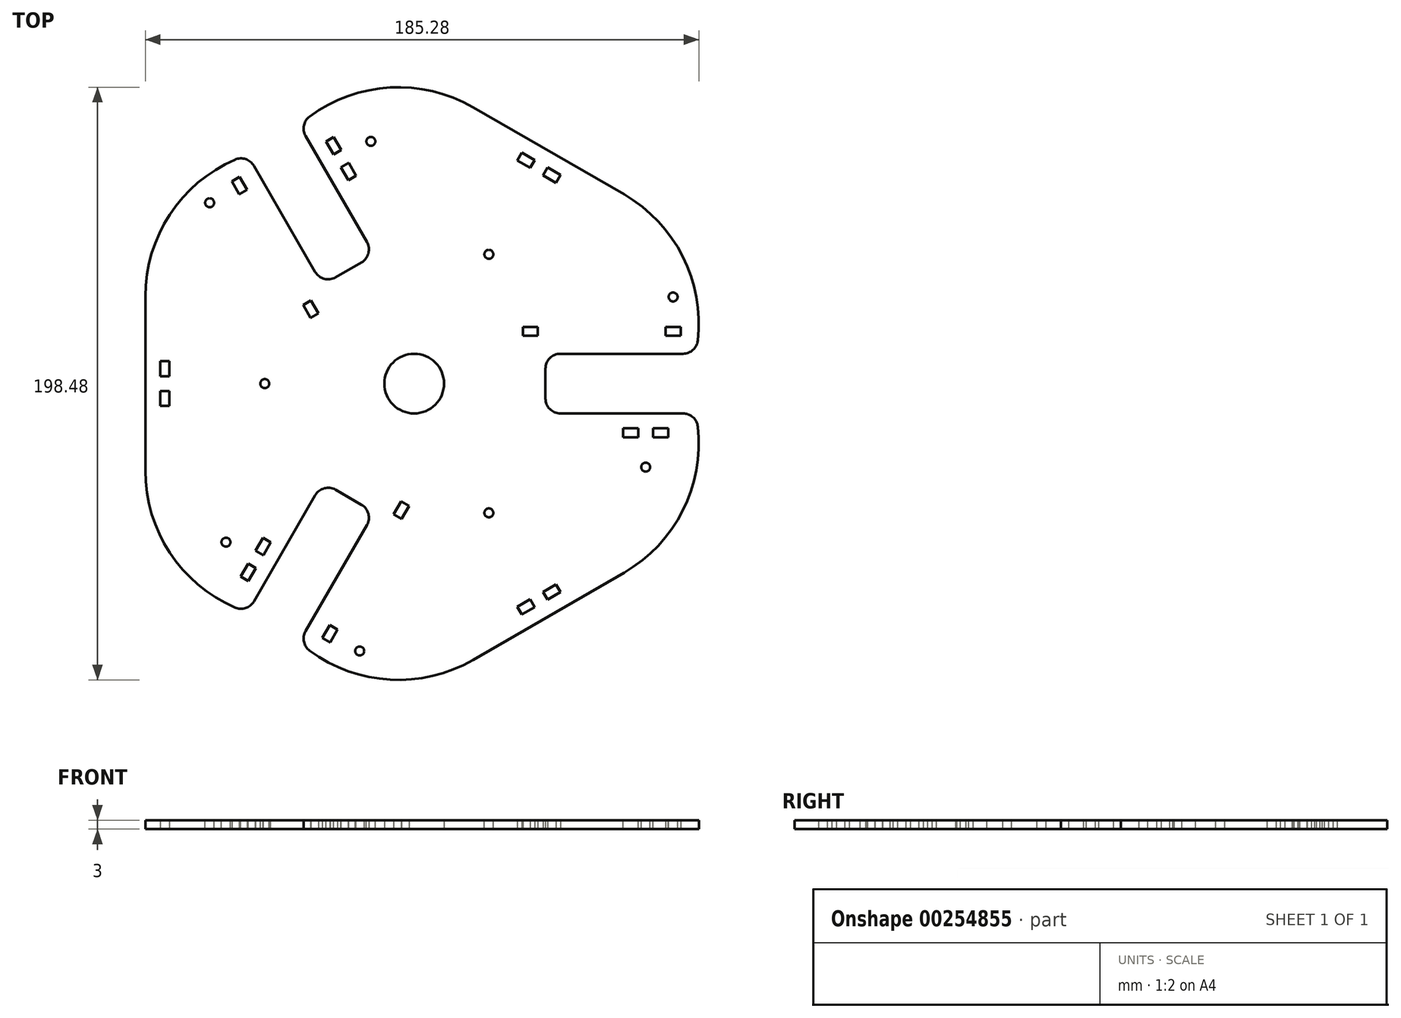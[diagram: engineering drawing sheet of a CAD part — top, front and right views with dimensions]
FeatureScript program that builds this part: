
annotation { "Feature Type Name" : "Feature", "Feature Type Description" : "" }
export const myFeature = defineFeature(function(context is Context, id is Id, definition is map)
    precondition{}
    {
        {
            var Q0;
            Q0=qCreatedBy(makeId("Top.planeOp"),FACE);
            var sketch = newSketch(context, id + "F0", { "sketchPlane" : qUnion([Q0])});
            skLineSegment(sketch, "E0", {"start": v(19.85, 17.5) * mm, "end": v(153.53, 17.5) * mm, "construction": true});
            skLineSegment(sketch, "E1.bottom", {"start": v(41.39, 16) * mm, "end": v(36.39, 16) * mm});
            skLineSegment(sketch, "E1.top", {"start": v(41.39, 19) * mm, "end": v(36.39, 19) * mm});
            skLineSegment(sketch, "E1.left", {"start": v(41.39, 16) * mm, "end": v(41.39, 19) * mm});
            skLineSegment(sketch, "E1.right", {"start": v(36.39, 16) * mm, "end": v(36.39, 19) * mm});
            skPoint(sketch, "E1.middle", {"position": v(38.89, 17.5) * mm});
            skLineSegment(sketch, "E2.bottom", {"start": v(89.19, 16) * mm, "end": v(84.19, 16) * mm});
            skLineSegment(sketch, "E2.top", {"start": v(89.19, 19) * mm, "end": v(84.19, 19) * mm});
            skLineSegment(sketch, "E2.left", {"start": v(89.19, 16) * mm, "end": v(89.19, 19) * mm});
            skLineSegment(sketch, "E2.right", {"start": v(84.19, 16) * mm, "end": v(84.19, 19) * mm});
            skPoint(sketch, "E2.middle", {"position": v(86.69, 17.5) * mm});
            skLineSegment(sketch, "E3", {"start": v(90, 10) * mm, "end": v(48.96, 10) * mm});
            skLineSegment(sketch, "E4", {"start": v(43.96, 5) * mm, "end": v(43.96, -5) * mm});
            skLineSegment(sketch, "E5", {"start": v(48.96, -10) * mm, "end": v(90, -10) * mm});
            skPoint(sketch, "E6.visualSharp", {"position": v(43.96, 10) * mm});
            skArc(sketch, "E6.filletArc", {"start": v(48.96, 10) * mm, "mid": v(45.42, 8.54) * mm, "end": v(43.96, 5) * mm});
            skPoint(sketch, "E7.visualSharp", {"position": v(43.96, -10) * mm});
            skArc(sketch, "E7.filletArc", {"start": v(43.96, -5) * mm, "mid": v(45.42, -8.54) * mm, "end": v(48.96, -10) * mm});
            skPoint(sketch, "E8.visualSharp", {"position": v(94.4, 59.99) * mm});
            skArc(sketch, "E8.filletArc", {"start": v(94.97, 14.44) * mm, "mid": v(89.92, 42.57) * mm, "end": v(70.28, 63.34) * mm});
            skPoint(sketch, "E9.visualSharp", {"position": v(94.34, 10) * mm});
            skArc(sketch, "E9.filletArc", {"start": v(90, 10) * mm, "mid": v(93.33, 11.27) * mm, "end": v(94.97, 14.44) * mm});
            skPoint(sketch, "E10.visualSharp", {"position": v(102.08, -10) * mm});
            skArc(sketch, "E10.filletArc", {"start": v(94.97, -14.44) * mm, "mid": v(93.33, -11.27) * mm, "end": v(90, -10) * mm});
            skLineSegment(sketch, "E11", {"start": v(0, 0) * mm, "end": v(57.44, 99.5) * mm, "construction": true});
            skLineSegment(sketch, "E12", {"start": v(0, 0) * mm, "end": v(55.62, -96.34) * mm, "construction": true});
            skLineSegment(sketch, "E13", {"start": v(70.28, -63.34) * mm, "end": v(45, -77.94) * mm});
            skLineSegment(sketch, "E14", {"start": v(70.28, 63.34) * mm, "end": v(45, 77.94) * mm});
            skPoint(sketch, "E15.visualSharp", {"position": v(93.21, -50.1) * mm});
            skArc(sketch, "E15.filletArc", {"start": v(70.28, -63.34) * mm, "mid": v(89.92, -42.57) * mm, "end": v(94.97, -14.44) * mm});
            skLineSegment(sketch, "E16.1.0", {"start": v(-90, 29.2) * mm, "end": v(-90, 0) * mm});
            skArc(sketch, "E16.1.1", {"start": v(-59.99, 75.03) * mm, "mid": v(-81.83, 56.59) * mm, "end": v(-90, 29.2) * mm});
            skArc(sketch, "E16.1.2", {"start": v(-53.66, 72.94) * mm, "mid": v(-56.43, 75.2) * mm, "end": v(-59.99, 75.03) * mm});
            skLineSegment(sketch, "E16.1.3", {"start": v(-53.66, 72.94) * mm, "end": v(-33.14, 37.4) * mm});
            skArc(sketch, "E16.1.4", {"start": v(-33.14, 37.4) * mm, "mid": v(-30.1, 35.07) * mm, "end": v(-26.3, 35.57) * mm});
            skLineSegment(sketch, "E16.1.5", {"start": v(-26.3, 35.57) * mm, "end": v(-17.65, 40.57) * mm});
            skArc(sketch, "E16.1.6", {"start": v(-17.65, 40.57) * mm, "mid": v(-15.32, 43.6) * mm, "end": v(-15.82, 47.4) * mm});
            skLineSegment(sketch, "E16.1.7", {"start": v(-15.82, 47.4) * mm, "end": v(-36.34, 82.94) * mm});
            skArc(sketch, "E16.1.8", {"start": v(19.72, 92.54) * mm, "mid": v(-8.09, 99.16) * mm, "end": v(-34.98, 89.46) * mm});
            skArc(sketch, "E16.1.9", {"start": v(-34.98, 89.46) * mm, "mid": v(-36.9, 86.46) * mm, "end": v(-36.34, 82.94) * mm});
            skLineSegment(sketch, "E16.1.10", {"start": v(-58.45, 69.24) * mm, "end": v(-55.95, 64.91) * mm});
            skLineSegment(sketch, "E16.1.11", {"start": v(-55.95, 64.91) * mm, "end": v(-58.55, 63.41) * mm});
            skLineSegment(sketch, "E16.1.12", {"start": v(-61.05, 67.74) * mm, "end": v(-58.55, 63.41) * mm});
            skLineSegment(sketch, "E16.1.13", {"start": v(-58.45, 69.24) * mm, "end": v(-61.05, 67.74) * mm});
            skLineSegment(sketch, "E16.1.14", {"start": v(-34.55, 27.84) * mm, "end": v(-37.15, 26.34) * mm});
            skLineSegment(sketch, "E16.1.15", {"start": v(-34.55, 27.84) * mm, "end": v(-32.05, 23.51) * mm});
            skLineSegment(sketch, "E16.1.16", {"start": v(-32.05, 23.51) * mm, "end": v(-34.65, 22.01) * mm});
            skLineSegment(sketch, "E16.1.17", {"start": v(-37.15, 26.34) * mm, "end": v(-34.65, 22.01) * mm});
            skLineSegment(sketch, "E16.1.18", {"start": v(19.72, 92.54) * mm, "end": v(45, 77.94) * mm});
            skLineSegment(sketch, "E16.2.0", {"start": v(19.72, -92.54) * mm, "end": v(45, -77.94) * mm});
            skArc(sketch, "E16.2.1", {"start": v(-34.98, -89.46) * mm, "mid": v(-8.09, -99.16) * mm, "end": v(19.72, -92.54) * mm});
            skArc(sketch, "E16.2.2", {"start": v(-36.34, -82.94) * mm, "mid": v(-36.9, -86.46) * mm, "end": v(-34.98, -89.46) * mm});
            skLineSegment(sketch, "E16.2.3", {"start": v(-36.34, -82.94) * mm, "end": v(-15.82, -47.4) * mm});
            skArc(sketch, "E16.2.4", {"start": v(-15.82, -47.4) * mm, "mid": v(-15.32, -43.6) * mm, "end": v(-17.65, -40.57) * mm});
            skLineSegment(sketch, "E16.2.5", {"start": v(-17.65, -40.57) * mm, "end": v(-26.3, -35.57) * mm});
            skArc(sketch, "E16.2.6", {"start": v(-26.3, -35.57) * mm, "mid": v(-30.1, -35.07) * mm, "end": v(-33.14, -37.4) * mm});
            skLineSegment(sketch, "E16.2.7", {"start": v(-33.14, -37.4) * mm, "end": v(-53.66, -72.94) * mm});
            skArc(sketch, "E16.2.8", {"start": v(-90, -29.2) * mm, "mid": v(-81.83, -56.59) * mm, "end": v(-59.99, -75.03) * mm});
            skArc(sketch, "E16.2.9", {"start": v(-59.99, -75.03) * mm, "mid": v(-56.43, -75.2) * mm, "end": v(-53.66, -72.94) * mm});
            skLineSegment(sketch, "E16.2.10", {"start": v(-30.74, -85.24) * mm, "end": v(-28.24, -80.91) * mm});
            skLineSegment(sketch, "E16.2.11", {"start": v(-28.24, -80.91) * mm, "end": v(-25.64, -82.41) * mm});
            skLineSegment(sketch, "E16.2.12", {"start": v(-28.14, -86.74) * mm, "end": v(-25.64, -82.41) * mm});
            skLineSegment(sketch, "E16.2.13", {"start": v(-30.74, -85.24) * mm, "end": v(-28.14, -86.74) * mm});
            skLineSegment(sketch, "E16.2.14", {"start": v(-6.84, -43.84) * mm, "end": v(-4.24, -45.34) * mm});
            skLineSegment(sketch, "E16.2.15", {"start": v(-6.84, -43.84) * mm, "end": v(-4.34, -39.51) * mm});
            skLineSegment(sketch, "E16.2.16", {"start": v(-4.34, -39.51) * mm, "end": v(-1.74, -41.01) * mm});
            skLineSegment(sketch, "E16.2.17", {"start": v(-4.24, -45.34) * mm, "end": v(-1.74, -41.01) * mm});
            skLineSegment(sketch, "E16.2.18", {"start": v(-90, -29.2) * mm, "end": v(-90, 0) * mm});
            skPoint(sketch, "E16.center", {"position": v(0, 0) * mm});
            skCircle(sketch, "E17", {"center": v(0, 0) * mm, "radius": 10 * mm});
            skLineSegment(sketch, "E18.bottom", {"start": v(-85, 7.5) * mm, "end": v(-82, 7.5) * mm});
            skLineSegment(sketch, "E18.top", {"start": v(-85, 2.5) * mm, "end": v(-82, 2.5) * mm});
            skLineSegment(sketch, "E18.left", {"start": v(-85, 7.5) * mm, "end": v(-85, 2.5) * mm});
            skLineSegment(sketch, "E18.right", {"start": v(-82, 7.5) * mm, "end": v(-82, 2.5) * mm});
            skLineSegment(sketch, "E19.bottom", {"start": v(-85, -2.5) * mm, "end": v(-82, -2.5) * mm});
            skLineSegment(sketch, "E19.top", {"start": v(-85, -7.5) * mm, "end": v(-82, -7.5) * mm});
            skLineSegment(sketch, "E19.left", {"start": v(-85, -2.5) * mm, "end": v(-85, -7.5) * mm});
            skLineSegment(sketch, "E19.right", {"start": v(-82, -2.5) * mm, "end": v(-82, -7.5) * mm});
            skLineSegment(sketch, "E20.1.0", {"start": v(36, -77.36) * mm, "end": v(34.5, -74.76) * mm});
            skLineSegment(sketch, "E20.1.1", {"start": v(36, -77.36) * mm, "end": v(40.33, -74.86) * mm});
            skLineSegment(sketch, "E20.1.2", {"start": v(34.5, -74.76) * mm, "end": v(38.83, -72.26) * mm});
            skLineSegment(sketch, "E20.1.3", {"start": v(40.33, -74.86) * mm, "end": v(38.83, -72.26) * mm});
            skLineSegment(sketch, "E20.1.4", {"start": v(44.67, -72.36) * mm, "end": v(43.17, -69.76) * mm});
            skLineSegment(sketch, "E20.1.5", {"start": v(44.67, -72.36) * mm, "end": v(49, -69.86) * mm});
            skLineSegment(sketch, "E20.1.6", {"start": v(49, -69.86) * mm, "end": v(47.5, -67.26) * mm});
            skLineSegment(sketch, "E20.1.7", {"start": v(43.17, -69.76) * mm, "end": v(47.5, -67.26) * mm});
            skLineSegment(sketch, "E20.2.0", {"start": v(49, 69.86) * mm, "end": v(47.5, 67.26) * mm});
            skLineSegment(sketch, "E20.2.1", {"start": v(49, 69.86) * mm, "end": v(44.67, 72.36) * mm});
            skLineSegment(sketch, "E20.2.2", {"start": v(47.5, 67.26) * mm, "end": v(43.17, 69.76) * mm});
            skLineSegment(sketch, "E20.2.3", {"start": v(44.67, 72.36) * mm, "end": v(43.17, 69.76) * mm});
            skLineSegment(sketch, "E20.2.4", {"start": v(40.33, 74.86) * mm, "end": v(38.83, 72.26) * mm});
            skLineSegment(sketch, "E20.2.5", {"start": v(40.33, 74.86) * mm, "end": v(36, 77.36) * mm});
            skLineSegment(sketch, "E20.2.6", {"start": v(36, 77.36) * mm, "end": v(34.5, 74.76) * mm});
            skLineSegment(sketch, "E20.2.7", {"start": v(38.83, 72.26) * mm, "end": v(34.5, 74.76) * mm});
            skSolve(sketch);
        }
        {
            var Q0;
            Q0 = qSketchRegion(id + "F0", true);
            extrude(context, id + "F1", {"entities" : qUnion([Q0]), "depth" : 3 * mm});
        }
        {
            var Q0;
            Q0=makeQuery(id+"F1.opExtrude","CAP_FACE",FACE,{"disambiguationData":[OSD([sQuery(id+"F0.wireOp",EDGE,"E1.bottom"),sQuery(id+"F0.wireOp",EDGE,"E1.top"),sQuery(id+"F0.wireOp",EDGE,"E1.left"),sQuery(id+"F0.wireOp",EDGE,"E1.right"),sQuery(id+"F0.wireOp",EDGE,"E2.bottom"),sQuery(id+"F0.wireOp",EDGE,"E2.top"),sQuery(id+"F0.wireOp",EDGE,"E2.left"),sQuery(id+"F0.wireOp",EDGE,"E2.right"),sQuery(id+"F0.wireOp",EDGE,"E3"),sQuery(id+"F0.wireOp",EDGE,"E4"),sQuery(id+"F0.wireOp",EDGE,"E5"),sQuery(id+"F0.wireOp",EDGE,"E6.filletArc"),sQuery(id+"F0.wireOp",EDGE,"E7.filletArc"),sQuery(id+"F0.wireOp",EDGE,"E8.filletArc"),sQuery(id+"F0.wireOp",EDGE,"E9.filletArc"),sQuery(id+"F0.wireOp",EDGE,"E10.filletArc"),sQuery(id+"F0.wireOp",EDGE,"E13"),sQuery(id+"F0.wireOp",EDGE,"E14"),sQuery(id+"F0.wireOp",EDGE,"E15.filletArc"),sQuery(id+"F0.wireOp",EDGE,"E16.1.0"),sQuery(id+"F0.wireOp",EDGE,"E16.1.1"),sQuery(id+"F0.wireOp",EDGE,"E16.1.2"),sQuery(id+"F0.wireOp",EDGE,"E16.1.3"),sQuery(id+"F0.wireOp",EDGE,"E16.1.4"),sQuery(id+"F0.wireOp",EDGE,"E16.1.5"),sQuery(id+"F0.wireOp",EDGE,"E16.1.6"),sQuery(id+"F0.wireOp",EDGE,"E16.1.7"),sQuery(id+"F0.wireOp",EDGE,"E16.1.8"),sQuery(id+"F0.wireOp",EDGE,"E16.1.9"),sQuery(id+"F0.wireOp",EDGE,"E16.1.10"),sQuery(id+"F0.wireOp",EDGE,"E16.1.11"),sQuery(id+"F0.wireOp",EDGE,"E16.1.12"),sQuery(id+"F0.wireOp",EDGE,"E16.1.13"),sQuery(id+"F0.wireOp",EDGE,"E16.1.14"),sQuery(id+"F0.wireOp",EDGE,"E16.1.15"),sQuery(id+"F0.wireOp",EDGE,"E16.1.16"),sQuery(id+"F0.wireOp",EDGE,"E16.1.17"),sQuery(id+"F0.wireOp",EDGE,"E16.1.18"),sQuery(id+"F0.wireOp",EDGE,"E16.2.0"),sQuery(id+"F0.wireOp",EDGE,"E16.2.1"),sQuery(id+"F0.wireOp",EDGE,"E16.2.2"),sQuery(id+"F0.wireOp",EDGE,"E16.2.3"),sQuery(id+"F0.wireOp",EDGE,"E16.2.4"),sQuery(id+"F0.wireOp",EDGE,"E16.2.5"),sQuery(id+"F0.wireOp",EDGE,"E16.2.6"),sQuery(id+"F0.wireOp",EDGE,"E16.2.7"),sQuery(id+"F0.wireOp",EDGE,"E16.2.8"),sQuery(id+"F0.wireOp",EDGE,"E16.2.9"),sQuery(id+"F0.wireOp",EDGE,"E16.2.10"),sQuery(id+"F0.wireOp",EDGE,"E16.2.11"),sQuery(id+"F0.wireOp",EDGE,"E16.2.12"),sQuery(id+"F0.wireOp",EDGE,"E16.2.13"),sQuery(id+"F0.wireOp",EDGE,"E16.2.14"),sQuery(id+"F0.wireOp",EDGE,"E16.2.15"),sQuery(id+"F0.wireOp",EDGE,"E16.2.16"),sQuery(id+"F0.wireOp",EDGE,"E16.2.17"),sQuery(id+"F0.wireOp",EDGE,"E16.2.18"),sQuery(id+"F0.wireOp",EDGE,"E17"),sQuery(id+"F0.wireOp",EDGE,"E18.bottom"),sQuery(id+"F0.wireOp",EDGE,"E18.top"),sQuery(id+"F0.wireOp",EDGE,"E18.left"),sQuery(id+"F0.wireOp",EDGE,"E18.right"),sQuery(id+"F0.wireOp",EDGE,"E19.bottom"),sQuery(id+"F0.wireOp",EDGE,"E19.top"),sQuery(id+"F0.wireOp",EDGE,"E19.left"),sQuery(id+"F0.wireOp",EDGE,"E19.right"),sQuery(id+"F0.wireOp",EDGE,"E20.1.0"),sQuery(id+"F0.wireOp",EDGE,"E20.1.1"),sQuery(id+"F0.wireOp",EDGE,"E20.1.2"),sQuery(id+"F0.wireOp",EDGE,"E20.1.3"),sQuery(id+"F0.wireOp",EDGE,"E20.1.4"),sQuery(id+"F0.wireOp",EDGE,"E20.1.5"),sQuery(id+"F0.wireOp",EDGE,"E20.1.6"),sQuery(id+"F0.wireOp",EDGE,"E20.1.7"),sQuery(id+"F0.wireOp",EDGE,"E20.2.0"),sQuery(id+"F0.wireOp",EDGE,"E20.2.1"),sQuery(id+"F0.wireOp",EDGE,"E20.2.2"),sQuery(id+"F0.wireOp",EDGE,"E20.2.3"),sQuery(id+"F0.wireOp",EDGE,"E20.2.4"),sQuery(id+"F0.wireOp",EDGE,"E20.2.5"),sQuery(id+"F0.wireOp",EDGE,"E20.2.6"),sQuery(id+"F0.wireOp",EDGE,"E20.2.7")])],"isStart":false});
            var sketch = newSketch(context, id + "F2", { "sketchPlane" : qUnion([Q0])});
            skCircle(sketch, "E21", {"center": v(-50, 0) * mm, "radius": 1.5 * mm});
            skCircle(sketch, "E22.1.0", {"center": v(25, -43.3) * mm, "radius": 1.5 * mm});
            skCircle(sketch, "E22.2.0", {"center": v(25, 43.3) * mm, "radius": 1.5 * mm});
            skPoint(sketch, "E22.center", {"position": v(0, 0) * mm});
            skCircle(sketch, "E23", {"center": v(86.69, 29) * mm, "radius": 1.5 * mm});
            skPoint(sketch, "E23.centerSnap0", {"position": v(86.69, 19) * mm});
            skCircle(sketch, "E24.1.0", {"center": v(-68.46, 60.58) * mm, "radius": 1.5 * mm});
            skCircle(sketch, "E24.2.0", {"center": v(-18.23, -89.58) * mm, "radius": 1.5 * mm});
            skLineSegment(sketch, "E25.bottom", {"start": v(70, -15) * mm, "end": v(75, -15) * mm});
            skLineSegment(sketch, "E25.top", {"start": v(70, -18) * mm, "end": v(75, -18) * mm});
            skLineSegment(sketch, "E25.left", {"start": v(70, -15) * mm, "end": v(70, -18) * mm});
            skLineSegment(sketch, "E25.right", {"start": v(75, -15) * mm, "end": v(75, -18) * mm});
            skLineSegment(sketch, "E26.bottom", {"start": v(80, -15) * mm, "end": v(85, -15) * mm});
            skLineSegment(sketch, "E26.top", {"start": v(80, -18) * mm, "end": v(85, -18) * mm});
            skLineSegment(sketch, "E26.left", {"start": v(80, -15) * mm, "end": v(80, -18) * mm});
            skLineSegment(sketch, "E26.right", {"start": v(85, -15) * mm, "end": v(85, -18) * mm});
            skLineSegment(sketch, "E27.1.0", {"start": v(-22, 68.12) * mm, "end": v(-24.5, 72.45) * mm});
            skLineSegment(sketch, "E27.1.1", {"start": v(-22, 68.12) * mm, "end": v(-19.41, 69.62) * mm});
            skLineSegment(sketch, "E27.1.2", {"start": v(-19.41, 69.62) * mm, "end": v(-21.91, 73.95) * mm});
            skLineSegment(sketch, "E27.1.3", {"start": v(-24.5, 72.45) * mm, "end": v(-21.91, 73.95) * mm});
            skLineSegment(sketch, "E27.1.4", {"start": v(-27, 76.78) * mm, "end": v(-24.41, 78.28) * mm});
            skLineSegment(sketch, "E27.1.5", {"start": v(-27, 76.78) * mm, "end": v(-29.5, 81.11) * mm});
            skLineSegment(sketch, "E27.1.6", {"start": v(-29.5, 81.11) * mm, "end": v(-26.91, 82.61) * mm});
            skLineSegment(sketch, "E27.1.7", {"start": v(-24.41, 78.28) * mm, "end": v(-26.91, 82.61) * mm});
            skLineSegment(sketch, "E27.2.0", {"start": v(-48, -53.12) * mm, "end": v(-50.5, -57.45) * mm});
            skLineSegment(sketch, "E27.2.1", {"start": v(-48, -53.12) * mm, "end": v(-50.59, -51.62) * mm});
            skLineSegment(sketch, "E27.2.2", {"start": v(-50.59, -51.62) * mm, "end": v(-53.09, -55.95) * mm});
            skLineSegment(sketch, "E27.2.3", {"start": v(-50.5, -57.45) * mm, "end": v(-53.09, -55.95) * mm});
            skLineSegment(sketch, "E27.2.4", {"start": v(-53, -61.78) * mm, "end": v(-55.59, -60.28) * mm});
            skLineSegment(sketch, "E27.2.5", {"start": v(-53, -61.78) * mm, "end": v(-55.5, -66.11) * mm});
            skLineSegment(sketch, "E27.2.6", {"start": v(-55.5, -66.11) * mm, "end": v(-58.09, -64.61) * mm});
            skLineSegment(sketch, "E27.2.7", {"start": v(-55.59, -60.28) * mm, "end": v(-58.09, -64.61) * mm});
            skCircle(sketch, "E28", {"center": v(77.5, -28) * mm, "radius": 1.5 * mm});
            skCircle(sketch, "E29.1.0", {"center": v(-14.5, 81.12) * mm, "radius": 1.5 * mm});
            skCircle(sketch, "E29.2.0", {"center": v(-63, -53.12) * mm, "radius": 1.5 * mm});
            skSolve(sketch);
        }
        {
            var Q0;
            Q0 = qSketchRegion(id + "F2", true);
            extrude(context, id + "F3", {"entities" : qUnion([Q0]), "operationType" : NewBodyOperationType.REMOVE, "endBound" : BoundingType.UP_TO_NEXT, "oppositeDirection" : true, "depth" : 25 * mm});
        }
    });
